# Revit family: Door-Roll-Up-Woodfold-Curtain-Panel
name_source: partatom
category: Doors
units: mm (PartAtom-declared; Revit-internal decimal feet)

## family parameters
Always vertical = Yes
Classification Number = 23.30.10.17.27.11
Cut with Voids When Loaded = No
Room Calculation Point = No
Shared = No

## types (1)
- 144"x96"-Right Mounted Motor
    Assembly Code = B2030420
    Crank Gear Type = Crank Gear : Motorized
    Description = Woodfold Curtain Panel Roll Up Door
    Fascia Material = Wood - Woodfold - Birch
    Frame Finish = Wood - Woodfold - Birch
    Has Hand Crank Packout = Yes
    Has Left Mounted Motor = No
    Has Motorized Packout = No
    Has Rail Only = No
    Has Right Mounted Motor = Yes
    Height = 8' - 0"
    Manufacturer = Woodfold Mfg., Inc.
    Model = Curtain Panel Roll Up Door
    Operator Motor Box = Hood : Standard
    Panel Material = Wood - Woodfold - Birch - Slats
    Product Documentation Link = http://woodfold.com
    Product Page URL = http://woodfold.com
    URL = http://woodfold.com

## geometry (parser evidence)
native form markers: Blend x38, Sweep x21
no freeform markers — native parametric forms only
